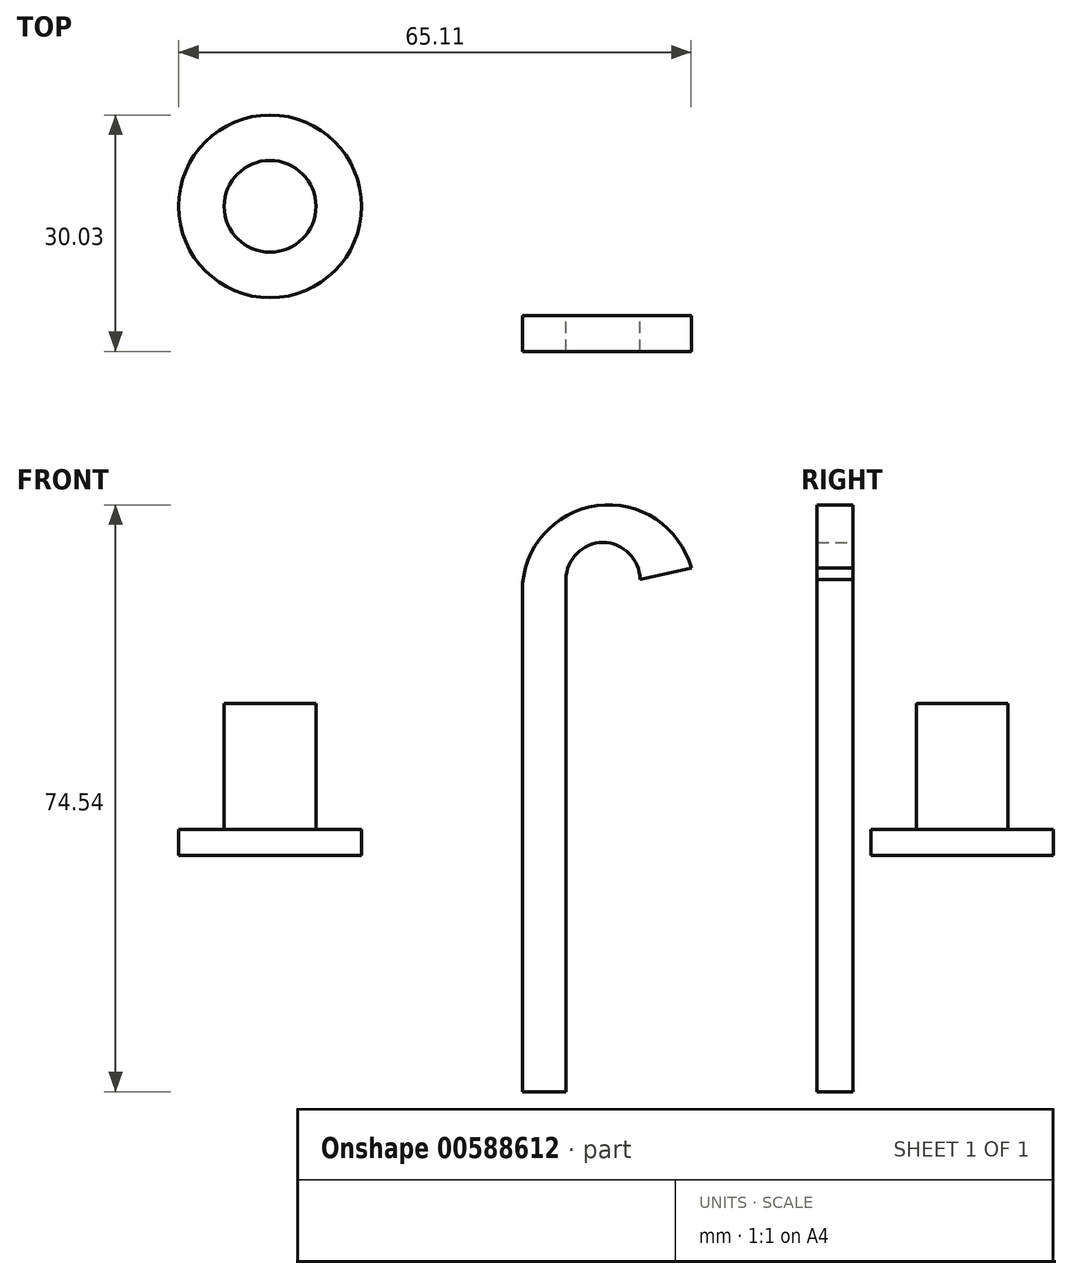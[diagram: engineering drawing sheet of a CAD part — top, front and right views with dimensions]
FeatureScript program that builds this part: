
annotation { "Feature Type Name" : "Feature", "Feature Type Description" : "" }
export const myFeature = defineFeature(function(context is Context, id is Id, definition is map)
    precondition{}
    {
        {
            var Q0;
            Q0=qCreatedBy(makeId("Front.planeOp"),FACE);
            var sketch = newSketch(context, id + "F0", { "sketchPlane" : qUnion([Q0])});
            skLineSegment(sketch, "E0", {"start": v(5.66, -10.24) * mm, "end": v(5.66, -30) * mm});
            skLineSegment(sketch, "E1", {"start": v(5.66, -30) * mm, "end": v(11.2, -30) * mm});
            skLineSegment(sketch, "E2", {"start": v(11.2, -30) * mm, "end": v(11.2, -10.48) * mm});
            skLineSegment(sketch, "E3", {"start": v(11.2, -10.48) * mm, "end": v(11.2, 16.03) * mm});
            skLineSegment(sketch, "E4", {"start": v(11.2, 16.03) * mm, "end": v(11.2, 35.06) * mm});
            skLineSegment(sketch, "E5", {"start": v(5.66, -10.24) * mm, "end": v(5.66, 16.27) * mm});
            skLineSegment(sketch, "E6", {"start": v(5.66, 16.27) * mm, "end": v(5.66, 33.62) * mm});
            skPoint(sketch, "E7.end.orphan", {"position": v(-3.25, 33.62) * mm});
            skPoint(sketch, "E7.start.orphan", {"position": v(-7.6, 35.06) * mm});
            skArc(sketch, "E8", {"start": v(27.11, 36.51) * mm, "mid": v(15.12, 44.44) * mm, "end": v(5.66, 33.62) * mm});
            skArc(sketch, "E9", {"start": v(20.6, 35.06) * mm, "mid": v(15.9, 39.76) * mm, "end": v(11.2, 35.06) * mm});
            skLineSegment(sketch, "E10", {"start": v(20.6, 35.06) * mm, "end": v(27.11, 36.51) * mm});
            skSolve(sketch);
        }
        {
            var Q0;
            Q0 = qSketchRegion(id + "F0", true);
            extrude(context, id + "F1", {"entities" : qUnion([Q0]), "depth" : 4.57 * mm, "offsetDistance" : 25.4 * mm});
        }
        {
            var Q0;
            Q0=qCreatedBy(makeId("Top.planeOp"),FACE);
            var sketch = newSketch(context, id + "F2", { "sketchPlane" : qUnion([Q0])});
            skCircle(sketch, "E11", {"center": v(-26.39, 13.86) * mm, "radius": 11.6 * mm});
            skSolve(sketch);
        }
        {
            var Q0;
            Q0 = qSketchRegion(id + "F2", true);
            extrude(context, id + "F3", {"entities" : qUnion([Q0]), "depth" : 3.3 * mm, "offsetDistance" : 25.4 * mm});
        }
        {
            var Q0;
            Q0=makeQuery(id+"F3.opExtrude","CAP_FACE",FACE,{"disambiguationData":[OSD([sQuery(id+"F2.wireOp",EDGE,"E11")])],"isStart":false});
            var sketch = newSketch(context, id + "F4", { "sketchPlane" : qUnion([Q0])});
            skCircle(sketch, "E12", {"center": v(-26.39, 13.86) * mm, "radius": 5.83 * mm});
            skSolve(sketch);
        }
        {
            var Q0;
            Q0 = qSketchRegion(id + "F4", true);
            extrude(context, id + "F5", {"entities" : qUnion([Q0]), "operationType" : NewBodyOperationType.ADD, "depth" : 16 * mm, "offsetDistance" : 25.4 * mm});
        }
    });
